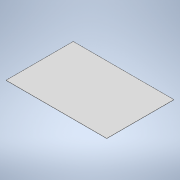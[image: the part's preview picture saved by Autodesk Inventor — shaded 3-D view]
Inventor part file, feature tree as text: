
AUTODESK INVENTOR PART (.ipt)
format: ipt  version: 2022 (Build 260153000, 153)  size: 96,256 bytes
history: native  units: mm
features: other x1, extrude x1, sketch x1
ambient origin geometry x8: Origin, YZ Plane, XZ Plane, XY Plane, X Axis, Y Axis, Z Axis, Center Point
bodies: Body1 (feature_tree)
feature tree (3):
  other  "Sólido1"
  extrude  "Extrusión1"  Depth=4000.0mm
  sketch  "Boceto1"  dims[d0=6000.0mm d1=4000.0mm d2=10.0mm d3=0.0mm]
